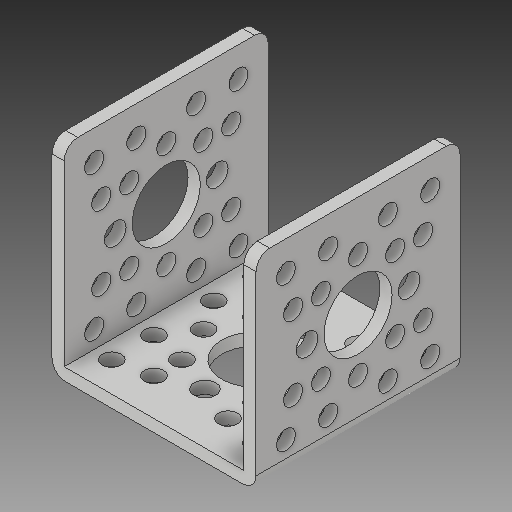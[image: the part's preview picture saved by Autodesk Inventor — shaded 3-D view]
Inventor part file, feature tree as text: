
AUTODESK INVENTOR PART (.ipt)
format: ipt  version: 2017 (Build 210142000, 142)  size: 310,272 bytes
history: native  units: in
note: dims shown in document units (in); Inventor stores cm internally (conversion verified against a paired STEP export)
features: mirror x1
ambient origin geometry x8: Origin, YZ Plane, XZ Plane, XY Plane, X Axis, Y Axis, Z Axis, Center Point
bodies: Solid1 (feature_tree)
feature tree (1):
  mirror  "Mirror9"
